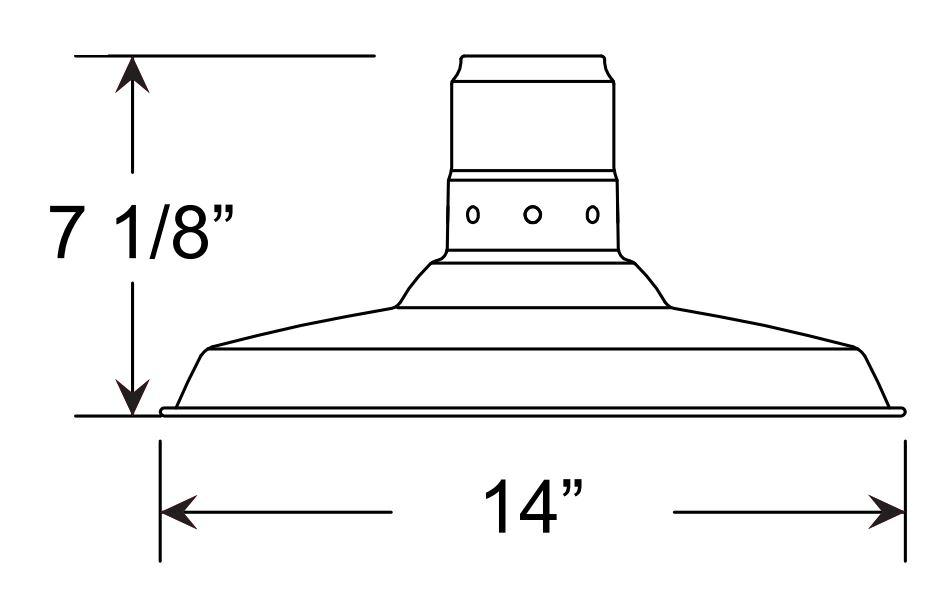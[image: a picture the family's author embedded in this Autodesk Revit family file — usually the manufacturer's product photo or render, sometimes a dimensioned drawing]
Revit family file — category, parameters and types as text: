
# Revit family: Vintage Emblem MU7
name_source: partatom
category: Lighting Fixtures
units: mm (PartAtom-declared; Revit-internal decimal feet)

## family parameters
Always vertical = Yes
Cut with Voids When Loaded = No
Light Source = Yes
OmniClass Number = 23.80.70.00
OmniClass Title = Lighting
Part Type = Normal
Room Calculation Point = No
Round Connector Dimension = Use Diameter
Shared = No
Work Plane-Based = No

## types (2) — shared parameters
Apparent Load = 200 VA
Body Colour = Spun aluminium
Body Material = body
CRI = >90
Color Filter = 16777215
Construction Material = Heavy Duty spun aluminum.
Default Elevation = 0' - 0"
Description = 120-277 Voltage
Dimming = 1%
Dimming Lamp Color Temperature Shift = <None>
Efficiency = 65-125 lumens per watt
Fixture Finish = Lilac
Inside body material = <By Category>
Lamp = 200W MAX INCANDESCENT
Life = L70 50,000 hours
Load Classification = Lighting
Manufacturer = ANP Lighting
Mounting Finish = Putty
Photometric Web File = generic.ies
Power Factor = 1
Tilt Angle = 90.00°
URL = https://www.anplighting.com
Voltage = 120 V
Warranty = 5 year limited warranty
Wattage Comments = 200W Max

## per-type parameters (varying)
| type | Fixture Diameter | Fixture Height | MU712 | MU714 | Weight |
| MU712 | 1' - 0" | 1' - 0" | Yes | No | 3.0 lb |
| MU714 | 1' - 2" | 1' - 1" | No | Yes | 4.0 lb |

note: column(s) folded — value = type name in every type: Model

## geometry (parser evidence)
native form markers: Sweep x25
no freeform markers — native parametric forms only
